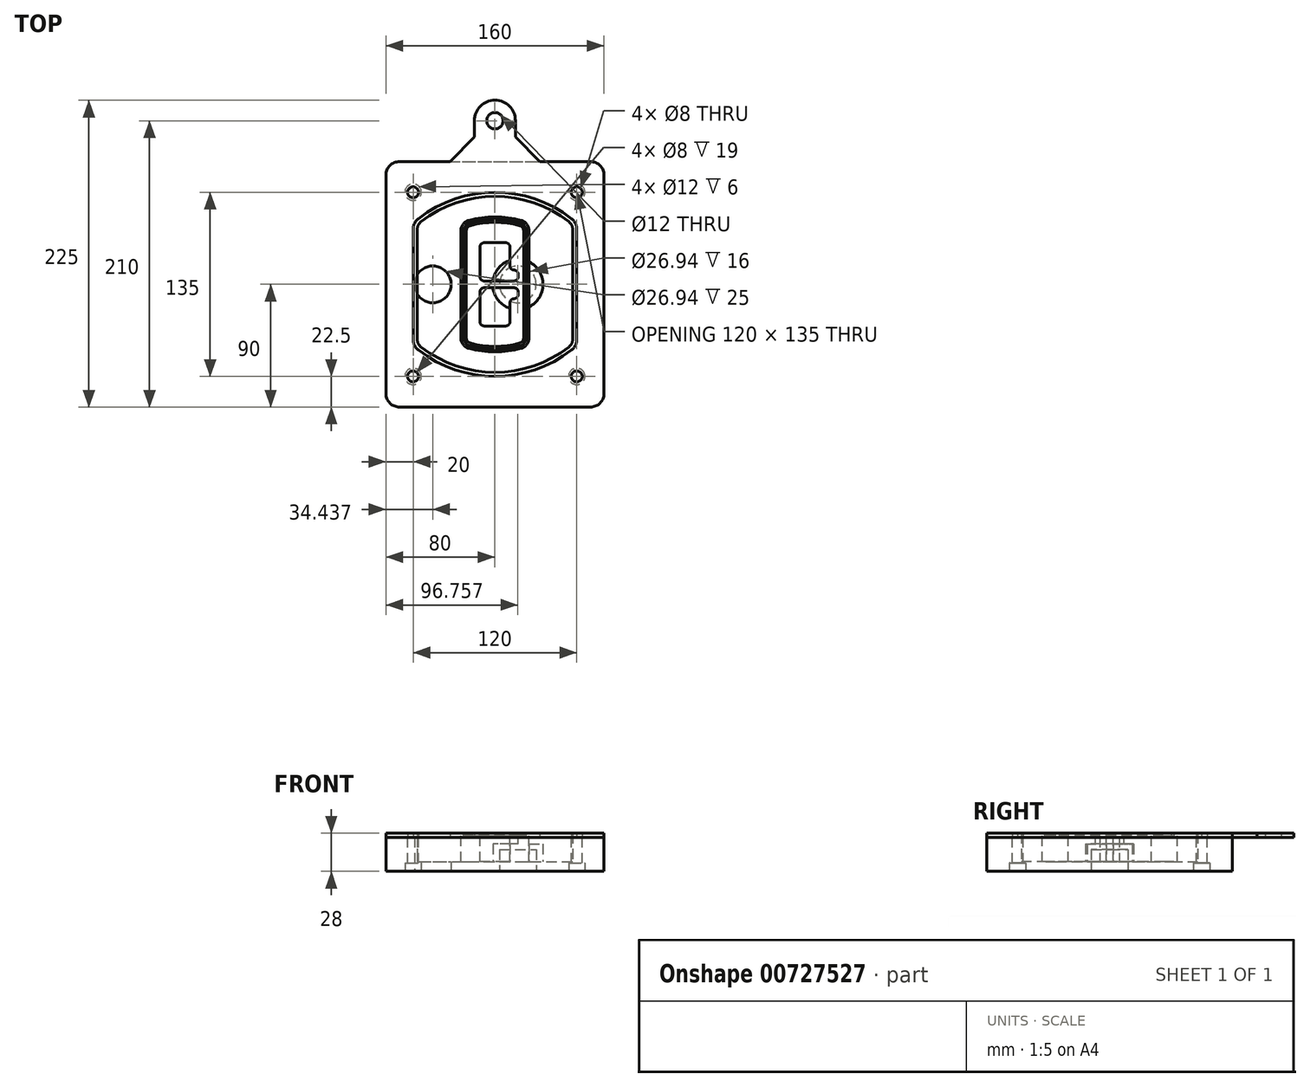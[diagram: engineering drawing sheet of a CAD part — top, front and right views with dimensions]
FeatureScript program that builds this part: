
annotation { "Feature Type Name" : "Feature", "Feature Type Description" : "" }
export const myFeature = defineFeature(function(context is Context, id is Id, definition is map)
    precondition{}
    {
        {
            var Q0;
            Q0=qCreatedBy(makeId("Top.planeOp"),FACE);
            var sketch = newSketch(context, id + "F0", { "sketchPlane" : qUnion([Q0])});
            skPoint(sketch, "E0.rect.middle", {"position": v(0, 0) * mm});
            skLineSegment(sketch, "E1.bottom", {"start": v(-70, -90) * mm, "end": v(70, -90) * mm});
            skLineSegment(sketch, "E1.top", {"start": v(-70, 90) * mm, "end": v(70, 90) * mm});
            skLineSegment(sketch, "E1.left", {"start": v(-80, -80) * mm, "end": v(-80, 80) * mm});
            skLineSegment(sketch, "E1.right", {"start": v(80, -80) * mm, "end": v(80, 80) * mm});
            skLineSegment(sketch, "E2", {"start": v(-80, 90) * mm, "end": v(80, -90) * mm, "construction": true});
            skLineSegment(sketch, "E3", {"start": v(80, 90) * mm, "end": v(-80, -90) * mm, "construction": true});
            skCircle(sketch, "E4", {"center": v(-60, 67.5) * mm, "radius": 4 * mm});
            skCircle(sketch, "E5", {"center": v(60, 67.5) * mm, "radius": 4 * mm});
            skCircle(sketch, "E6", {"center": v(60, -67.5) * mm, "radius": 4 * mm});
            skCircle(sketch, "E7", {"center": v(-60, -67.5) * mm, "radius": 4 * mm});
            skLineSegment(sketch, "E8", {"start": v(-60, 67.5) * mm, "end": v(60, 67.5) * mm, "construction": true});
            skLineSegment(sketch, "E9", {"start": v(60, 67.5) * mm, "end": v(60, -67.5) * mm, "construction": true});
            skLineSegment(sketch, "E10", {"start": v(60, -67.5) * mm, "end": v(-60, -67.5) * mm, "construction": true});
            skLineSegment(sketch, "E11", {"start": v(-60, -67.5) * mm, "end": v(-60, 67.5) * mm, "construction": true});
            skLineSegment(sketch, "E12", {"start": v(-60, 40.3) * mm, "end": v(-60, -40.3) * mm});
            skLineSegment(sketch, "E13", {"start": v(60, 40.3) * mm, "end": v(60, -40.3) * mm});
            skArc(sketch, "E14", {"start": v(56.15, 48.18) * mm, "mid": v(0, 67.5) * mm, "end": v(-56.15, 48.18) * mm});
            skArc(sketch, "E15", {"start": v(-56.15, -48.18) * mm, "mid": v(0, -67.5) * mm, "end": v(56.15, -48.18) * mm});
            skLineSegment(sketch, "E16", {"start": v(-60, 0) * mm, "end": v(60, 0) * mm, "construction": true});
            skPoint(sketch, "E17.visualSharp", {"position": v(-60, -45) * mm});
            skArc(sketch, "E17.filletArc", {"start": v(-60, -40.3) * mm, "mid": v(-58.99, -44.68) * mm, "end": v(-56.15, -48.18) * mm});
            skPoint(sketch, "E18.visualSharp", {"position": v(-60, 45) * mm});
            skArc(sketch, "E18.filletArc", {"start": v(-56.15, 48.18) * mm, "mid": v(-58.99, 44.68) * mm, "end": v(-60, 40.3) * mm});
            skPoint(sketch, "E19.visualSharp", {"position": v(60, 45) * mm});
            skArc(sketch, "E19.filletArc", {"start": v(60, 40.3) * mm, "mid": v(58.99, 44.68) * mm, "end": v(56.15, 48.18) * mm});
            skPoint(sketch, "E20.visualSharp", {"position": v(60, -45) * mm});
            skArc(sketch, "E20.filletArc", {"start": v(56.15, -48.18) * mm, "mid": v(58.99, -44.68) * mm, "end": v(60, -40.3) * mm});
            skPoint(sketch, "E21.visualSharp", {"position": v(-80, 90) * mm});
            skArc(sketch, "E21.filletArc", {"start": v(-70, 90) * mm, "mid": v(-77.07, 87.07) * mm, "end": v(-80, 80) * mm});
            skPoint(sketch, "E22.visualSharp", {"position": v(80, 90) * mm});
            skArc(sketch, "E22.filletArc", {"start": v(80, 80) * mm, "mid": v(77.07, 87.07) * mm, "end": v(70, 90) * mm});
            skPoint(sketch, "E23.visualSharp", {"position": v(80, -90) * mm});
            skArc(sketch, "E23.filletArc", {"start": v(70, -90) * mm, "mid": v(77.07, -87.07) * mm, "end": v(80, -80) * mm});
            skPoint(sketch, "E24.visualSharp", {"position": v(-80, -90) * mm});
            skArc(sketch, "E24.filletArc", {"start": v(-80, -80) * mm, "mid": v(-77.07, -87.07) * mm, "end": v(-70, -90) * mm});
            skArc(sketch, "E25.0", {"start": v(57, 40.3) * mm, "mid": v(56.3, 43.36) * mm, "end": v(54.3, 45.81) * mm});
            skLineSegment(sketch, "E25.1", {"start": v(57, 40.3) * mm, "end": v(57, -40.3) * mm});
            skArc(sketch, "E25.2", {"start": v(54.3, -45.81) * mm, "mid": v(56.3, -43.36) * mm, "end": v(57, -40.3) * mm});
            skArc(sketch, "E25.3", {"start": v(-54.3, -45.81) * mm, "mid": v(0, -64.5) * mm, "end": v(54.3, -45.81) * mm});
            skArc(sketch, "E25.4", {"start": v(-57, -40.3) * mm, "mid": v(-56.3, -43.36) * mm, "end": v(-54.3, -45.81) * mm});
            skArc(sketch, "E25.5", {"start": v(54.3, 45.81) * mm, "mid": v(0, 64.5) * mm, "end": v(-54.3, 45.81) * mm});
            skLineSegment(sketch, "E25.6", {"start": v(-57, 40.3) * mm, "end": v(-57, -40.3) * mm});
            skArc(sketch, "E25.7", {"start": v(-54.3, 45.81) * mm, "mid": v(-56.3, 43.36) * mm, "end": v(-57, 40.3) * mm});
            skArc(sketch, "E26.0", {"start": v(-58.62, 51.33) * mm, "mid": v(-62.58, 46.43) * mm, "end": v(-64, 40.3) * mm});
            skArc(sketch, "E26.1", {"start": v(58.62, 51.33) * mm, "mid": v(0, 71.5) * mm, "end": v(-58.62, 51.33) * mm});
            skArc(sketch, "E26.2", {"start": v(64, 40.3) * mm, "mid": v(62.58, 46.43) * mm, "end": v(58.62, 51.33) * mm});
            skLineSegment(sketch, "E26.3", {"start": v(64, 40.3) * mm, "end": v(64, -40.3) * mm});
            skArc(sketch, "E26.4", {"start": v(58.62, -51.33) * mm, "mid": v(62.58, -46.43) * mm, "end": v(64, -40.3) * mm});
            skLineSegment(sketch, "E26.5", {"start": v(-64, 40.3) * mm, "end": v(-64, -40.3) * mm});
            skArc(sketch, "E26.6", {"start": v(-58.62, -51.33) * mm, "mid": v(0, -71.5) * mm, "end": v(58.62, -51.33) * mm});
            skArc(sketch, "E26.7", {"start": v(-64, -40.3) * mm, "mid": v(-62.58, -46.43) * mm, "end": v(-58.62, -51.33) * mm});
            skSolve(sketch);
        }
        {
            var Q0;
            Q0=makeQuery(id+"F0.imprint","IMPRINT",FACE,{"disambiguationData":[TD([[makeQuery(id+"F0.imprint","IMPRINT",EDGE,{"derivedFrom":sQuery(id+"F0.wireOp",EDGE,"E1.bottom")}),1.0]])]});
            var Q1;
            Q1=makeQuery(id+"F0.imprint","IMPRINT",FACE,{"disambiguationData":[TD([[makeQuery(id+"F0.imprint","IMPRINT",EDGE,{"derivedFrom":sQuery(id+"F0.wireOp",EDGE,"E12")}),1.0]])]});
            var Q2;
            Q2=makeQuery(id+"F0.imprint","IMPRINT",FACE,{"disambiguationData":[TD([[makeQuery(id+"F0.imprint","IMPRINT",EDGE,{"derivedFrom":sQuery(id+"F0.wireOp",EDGE,"E25.0")}),1.0]])]});
            var Q3;
            Q3=makeQuery(id+"F0.imprint","IMPRINT",FACE,{"disambiguationData":[TD([[makeQuery(id+"F0.imprint","IMPRINT",EDGE,{"derivedFrom":sQuery(id+"F0.wireOp",EDGE,"E12")}),-1.0]])]});
            extrude(context, id + "F1", {"entities" : qUnion([Q0, Q1, Q2, Q3]), "oppositeDirection" : true, "depth" : 25 * mm});
        }
        {
            var Q0;
            Q0=makeQuery(id+"F0.imprint","IMPRINT",FACE,{"disambiguationData":[TD([[makeQuery(id+"F0.imprint","IMPRINT",EDGE,{"derivedFrom":sQuery(id+"F0.wireOp",EDGE,"E12")}),1.0]])]});
            extrude(context, id + "F2", {"entities" : qUnion([Q0]), "operationType" : NewBodyOperationType.ADD, "depth" : 3 * mm});
        }
        {
            var Q0;
            Q0=makeQuery(id+"F0.imprint","IMPRINT",FACE,{"disambiguationData":[TD([[makeQuery(id+"F0.imprint","IMPRINT",EDGE,{"derivedFrom":sQuery(id+"F0.wireOp",EDGE,"E25.0")}),1.0]])]});
            extrude(context, id + "F3", {"entities" : qUnion([Q0]), "operationType" : NewBodyOperationType.REMOVE, "oppositeDirection" : true, "depth" : 18 * mm});
        }
        {
            var Q0;
            Q0=makeQuery(id+"F2.opExtrude","CAP_FACE",FACE,{"disambiguationData":[OSD([sQuery(id+"F0.wireOp",EDGE,"E12"),sQuery(id+"F0.wireOp",EDGE,"E13"),sQuery(id+"F0.wireOp",EDGE,"E14"),sQuery(id+"F0.wireOp",EDGE,"E15"),sQuery(id+"F0.wireOp",EDGE,"E17.filletArc"),sQuery(id+"F0.wireOp",EDGE,"E18.filletArc"),sQuery(id+"F0.wireOp",EDGE,"E19.filletArc"),sQuery(id+"F0.wireOp",EDGE,"E20.filletArc"),sQuery(id+"F0.wireOp",EDGE,"E25.0"),sQuery(id+"F0.wireOp",EDGE,"E25.1"),sQuery(id+"F0.wireOp",EDGE,"E25.2"),sQuery(id+"F0.wireOp",EDGE,"E25.3"),sQuery(id+"F0.wireOp",EDGE,"E25.4"),sQuery(id+"F0.wireOp",EDGE,"E25.5"),sQuery(id+"F0.wireOp",EDGE,"E25.6"),sQuery(id+"F0.wireOp",EDGE,"E25.7")])],"isStart":false});
            var sketch = newSketch(context, id + "F4", { "sketchPlane" : qUnion([Q0])});
            skArc(sketch, "E27.0", {"start": v(-19.08, -46.97) * mm, "mid": v(0, -49.5) * mm, "end": v(19.08, -46.97) * mm});
            skArc(sketch, "E28.0", {"start": v(19.08, 46.97) * mm, "mid": v(0, 49.5) * mm, "end": v(-19.08, 46.97) * mm});
            skLineSegment(sketch, "E29", {"start": v(-25, 39.25) * mm, "end": v(-25, -39.25) * mm});
            skLineSegment(sketch, "E30", {"start": v(25, 39.25) * mm, "end": v(25, -39.25) * mm});
            skLineSegment(sketch, "E31", {"start": v(-25, 45.1) * mm, "end": v(25, 45.1) * mm, "construction": true});
            skLineSegment(sketch, "E32", {"start": v(-25, -45.1) * mm, "end": v(25, -45.1) * mm, "construction": true});
            skPoint(sketch, "E33.visualSharp", {"position": v(-25, 45.1) * mm});
            skArc(sketch, "E33.filletArc", {"start": v(-19.08, 46.97) * mm, "mid": v(-23.35, 44.11) * mm, "end": v(-25, 39.25) * mm});
            skPoint(sketch, "E34.visualSharp", {"position": v(25, 45.1) * mm});
            skArc(sketch, "E34.filletArc", {"start": v(25, 39.25) * mm, "mid": v(23.35, 44.11) * mm, "end": v(19.08, 46.97) * mm});
            skPoint(sketch, "E35.visualSharp", {"position": v(25, -45.1) * mm});
            skArc(sketch, "E35.filletArc", {"start": v(19.08, -46.97) * mm, "mid": v(23.35, -44.11) * mm, "end": v(25, -39.25) * mm});
            skPoint(sketch, "E36.visualSharp", {"position": v(-25, -45.1) * mm});
            skArc(sketch, "E36.filletArc", {"start": v(-25, -39.25) * mm, "mid": v(-23.35, -44.11) * mm, "end": v(-19.08, -46.97) * mm});
            skArc(sketch, "E37.0", {"start": v(54.3, 45.81) * mm, "mid": v(0, 64.5) * mm, "end": v(-54.3, 45.81) * mm});
            skArc(sketch, "E37.1", {"start": v(-54.3, 45.81) * mm, "mid": v(-56.3, 43.36) * mm, "end": v(-57, 40.3) * mm});
            skLineSegment(sketch, "E37.2", {"start": v(-57, 40.3) * mm, "end": v(-57, -40.3) * mm});
            skArc(sketch, "E37.3", {"start": v(-57, -40.3) * mm, "mid": v(-56.3, -43.36) * mm, "end": v(-54.3, -45.81) * mm});
            skArc(sketch, "E37.4", {"start": v(-54.3, -45.81) * mm, "mid": v(0, -64.5) * mm, "end": v(54.3, -45.81) * mm});
            skArc(sketch, "E37.5", {"start": v(54.3, -45.81) * mm, "mid": v(56.3, -43.36) * mm, "end": v(57, -40.3) * mm});
            skLineSegment(sketch, "E37.6", {"start": v(57, 40.3) * mm, "end": v(57, -40.3) * mm});
            skArc(sketch, "E37.7", {"start": v(57, 40.3) * mm, "mid": v(56.3, 43.36) * mm, "end": v(54.3, 45.81) * mm});
            skLineSegment(sketch, "E38.0", {"start": v(23, 39.25) * mm, "end": v(23, -39.25) * mm});
            skArc(sketch, "E38.1", {"start": v(18.56, -45.04) * mm, "mid": v(21.76, -42.9) * mm, "end": v(23, -39.25) * mm});
            skArc(sketch, "E38.2", {"start": v(-18.56, -45.04) * mm, "mid": v(0, -47.5) * mm, "end": v(18.56, -45.04) * mm});
            skArc(sketch, "E38.3", {"start": v(-23, -39.25) * mm, "mid": v(-21.76, -42.9) * mm, "end": v(-18.56, -45.04) * mm});
            skLineSegment(sketch, "E38.4", {"start": v(-23, 39.25) * mm, "end": v(-23, -39.25) * mm});
            skArc(sketch, "E38.5", {"start": v(23, 39.25) * mm, "mid": v(21.76, 42.9) * mm, "end": v(18.56, 45.04) * mm});
            skArc(sketch, "E38.6", {"start": v(-18.56, 45.04) * mm, "mid": v(-21.76, 42.9) * mm, "end": v(-23, 39.25) * mm});
            skArc(sketch, "E38.7", {"start": v(18.56, 45.04) * mm, "mid": v(0, 47.5) * mm, "end": v(-18.56, 45.04) * mm});
            skArc(sketch, "E39.0", {"start": v(21, 39.25) * mm, "mid": v(20.18, 41.68) * mm, "end": v(18.04, 43.1) * mm});
            skLineSegment(sketch, "E39.1", {"start": v(21, 39.25) * mm, "end": v(21, -39.25) * mm});
            skArc(sketch, "E39.2", {"start": v(18.04, -43.1) * mm, "mid": v(20.18, -41.68) * mm, "end": v(21, -39.25) * mm});
            skArc(sketch, "E39.3", {"start": v(-18.04, -43.1) * mm, "mid": v(0, -45.5) * mm, "end": v(18.04, -43.1) * mm});
            skArc(sketch, "E39.4", {"start": v(-21, -39.25) * mm, "mid": v(-20.18, -41.68) * mm, "end": v(-18.04, -43.1) * mm});
            skArc(sketch, "E39.5", {"start": v(18.04, 43.1) * mm, "mid": v(0, 45.5) * mm, "end": v(-18.04, 43.1) * mm});
            skLineSegment(sketch, "E39.6", {"start": v(-21, 39.25) * mm, "end": v(-21, -39.25) * mm});
            skArc(sketch, "E39.7", {"start": v(-18.04, 43.1) * mm, "mid": v(-20.18, 41.68) * mm, "end": v(-21, 39.25) * mm});
            skLineSegment(sketch, "E40", {"start": v(-25, 0) * mm, "end": v(25, 0) * mm, "construction": true});
            skLineSegment(sketch, "E41", {"start": v(-11, 5.5) * mm, "end": v(-11, 27.5) * mm});
            skLineSegment(sketch, "E42", {"start": v(-8, 30.5) * mm, "end": v(8, 30.5) * mm});
            skLineSegment(sketch, "E43", {"start": v(11, 27.5) * mm, "end": v(11, 13.5) * mm});
            skLineSegment(sketch, "E44", {"start": v(14, 10.5) * mm, "end": v(14, 10.5) * mm});
            skLineSegment(sketch, "E45", {"start": v(17, 7.5) * mm, "end": v(17, 5.5) * mm});
            skLineSegment(sketch, "E46", {"start": v(14, 2.5) * mm, "end": v(-8, 2.5) * mm});
            skPoint(sketch, "E47.visualSharp", {"position": v(-11, 30.5) * mm});
            skArc(sketch, "E47.filletArc", {"start": v(-8, 30.5) * mm, "mid": v(-10.12, 29.62) * mm, "end": v(-11, 27.5) * mm});
            skPoint(sketch, "E48.visualSharp", {"position": v(11, 30.5) * mm});
            skArc(sketch, "E48.filletArc", {"start": v(11, 27.5) * mm, "mid": v(10.12, 29.62) * mm, "end": v(8, 30.5) * mm});
            skPoint(sketch, "E49.visualSharp", {"position": v(11, 10.5) * mm});
            skArc(sketch, "E49.filletArc", {"start": v(11, 13.5) * mm, "mid": v(11.88, 11.38) * mm, "end": v(14, 10.5) * mm});
            skPoint(sketch, "E50.visualSharp", {"position": v(17, 10.5) * mm});
            skArc(sketch, "E50.filletArc", {"start": v(17, 7.5) * mm, "mid": v(16.12, 9.62) * mm, "end": v(14, 10.5) * mm});
            skPoint(sketch, "E51.visualSharp", {"position": v(17, 2.5) * mm});
            skArc(sketch, "E51.filletArc", {"start": v(14, 2.5) * mm, "mid": v(16.12, 3.38) * mm, "end": v(17, 5.5) * mm});
            skPoint(sketch, "E52.visualSharp", {"position": v(-11, 2.5) * mm});
            skArc(sketch, "E52.filletArc", {"start": v(-11, 5.5) * mm, "mid": v(-10.12, 3.38) * mm, "end": v(-8, 2.5) * mm});
            skLineSegment(sketch, "E53.0.MirrorCS", {"start": v(14, -2.5) * mm, "end": v(-8, -2.5) * mm});
            skArc(sketch, "E54.0.MirrorCS", {"start": v(-11, -5.5) * mm, "mid": v(-10.12, -3.38) * mm, "end": v(-8, -2.5) * mm});
            skLineSegment(sketch, "E55.0.MirrorCS", {"start": v(-11, -5.5) * mm, "end": v(-11, -27.5) * mm});
            skArc(sketch, "E56.0.MirrorCS", {"start": v(-8, -30.5) * mm, "mid": v(-10.12, -29.62) * mm, "end": v(-11, -27.5) * mm});
            skLineSegment(sketch, "E57.0.MirrorCS", {"start": v(-8, -30.5) * mm, "end": v(8, -30.5) * mm});
            skArc(sketch, "E58.0.MirrorCS", {"start": v(11, -27.5) * mm, "mid": v(10.12, -29.62) * mm, "end": v(8, -30.5) * mm});
            skLineSegment(sketch, "E59.0.MirrorCS", {"start": v(11, -27.5) * mm, "end": v(11, -13.5) * mm});
            skArc(sketch, "E60.0.MirrorCS", {"start": v(11, -13.5) * mm, "mid": v(11.88, -11.38) * mm, "end": v(14, -10.5) * mm});
            skArc(sketch, "E61.0.MirrorCS", {"start": v(17, -7.5) * mm, "mid": v(16.12, -9.62) * mm, "end": v(14, -10.5) * mm});
            skLineSegment(sketch, "E62.0.MirrorCS", {"start": v(17, -7.5) * mm, "end": v(17, -5.5) * mm});
            skArc(sketch, "E63.0.MirrorCS", {"start": v(14, -2.5) * mm, "mid": v(16.12, -3.38) * mm, "end": v(17, -5.5) * mm});
            skSolve(sketch);
        }
        {
            var Q0;
            Q0=makeQuery(id+"F4.imprint","IMPRINT",FACE,{"disambiguationData":[TD([[makeQuery(id+"F4.imprint","IMPRINT",EDGE,{"derivedFrom":sQuery(id+"F4.wireOp",EDGE,"E27.0")}),1.0]])]});
            var Q1;
            Q1=makeQuery(id+"F4.imprint","IMPRINT",FACE,{"disambiguationData":[TD([[makeQuery(id+"F4.imprint","IMPRINT",EDGE,{"derivedFrom":sQuery(id+"F4.wireOp",EDGE,"E38.0")}),-1.0]])]});
            var Q2;
            Q2=makeQuery(id+"F4.imprint","IMPRINT",FACE,{"disambiguationData":[TD([[makeQuery(id+"F4.imprint","IMPRINT",EDGE,{"derivedFrom":sQuery(id+"F4.wireOp",EDGE,"E39.0")}),1.0]])]});
            extrude(context, id + "F5", {"entities" : qUnion([Q0, Q1, Q2]), "operationType" : NewBodyOperationType.ADD, "endBound" : BoundingType.UP_TO_NEXT, "oppositeDirection" : true, "depth" : 25 * mm});
        }
        {
            var Q0;
            Q0=makeQuery(id+"F4.imprint","IMPRINT",FACE,{"disambiguationData":[TD([[makeQuery(id+"F4.imprint","IMPRINT",EDGE,{"derivedFrom":sQuery(id+"F4.wireOp",EDGE,"E38.0")}),-1.0]])]});
            extrude(context, id + "F6", {"entities" : qUnion([Q0]), "operationType" : NewBodyOperationType.REMOVE, "oppositeDirection" : true, "depth" : 2 * mm});
        }
        {
            var Q0;
            Q0=makeQuery(id+"F1.opExtrude","CAP_FACE",FACE,{"disambiguationData":[OSD([sQuery(id+"F0.wireOp",EDGE,"E1.bottom"),sQuery(id+"F0.wireOp",EDGE,"E1.top"),sQuery(id+"F0.wireOp",EDGE,"E1.left"),sQuery(id+"F0.wireOp",EDGE,"E1.right"),sQuery(id+"F0.wireOp",EDGE,"E4"),sQuery(id+"F0.wireOp",EDGE,"E5"),sQuery(id+"F0.wireOp",EDGE,"E6"),sQuery(id+"F0.wireOp",EDGE,"E7"),sQuery(id+"F0.wireOp",EDGE,"E21.filletArc"),sQuery(id+"F0.wireOp",EDGE,"E22.filletArc"),sQuery(id+"F0.wireOp",EDGE,"E23.filletArc"),sQuery(id+"F0.wireOp",EDGE,"E24.filletArc")])],"isStart":false});
            var sketch = newSketch(context, id + "F7", { "sketchPlane" : qUnion([Q0])});
            skCircle(sketch, "E64", {"center": v(16.76, 0) * mm, "radius": 13.47 * mm});
            skCircle(sketch, "E65", {"center": v(-45.56, 0) * mm, "radius": 13.47 * mm});
            skLineSegment(sketch, "E66", {"start": v(80, 0) * mm, "end": v(-80, 0) * mm});
            skCircle(sketch, "E67", {"center": v(16.76, 0) * mm, "radius": 18.47 * mm});
            skCircle(sketch, "E68", {"center": v(60, -67.5) * mm, "radius": 6 * mm});
            skCircle(sketch, "E69", {"center": v(-60, -67.5) * mm, "radius": 6 * mm});
            skCircle(sketch, "E70", {"center": v(-60, 67.5) * mm, "radius": 6 * mm});
            skCircle(sketch, "E71", {"center": v(60, 67.5) * mm, "radius": 6 * mm});
            skSolve(sketch);
        }
        {
            var Q0;
            {var subQ1=sQuery(id+"F7.wireOp",EDGE,"E66");var subQ4=sQuery(id+"F7.wireOp",EDGE,"E64");var subQ6=makeQuery(id+"F7.imprint","INTERSECT",VERTEX,{"disambiguationData":[OD(0.0)],"derivedFrom":[subQ4,subQ1]});Q0=makeQuery(id+"F7.imprint","IMPRINT",FACE,{"disambiguationData":[TD([[makeQuery(id+"F7.imprint","IMPRINT",EDGE,{"disambiguationData":[TD([[subQ6,-1.0]])],"derivedFrom":subQ4}),-1.0]])]});}
            var Q1;
            {var subQ0=sQuery(id+"F7.wireOp",EDGE,"E66");var subQ1=sQuery(id+"F7.wireOp",EDGE,"E64");var subQ3=makeQuery(id+"F7.imprint","INTERSECT",VERTEX,{"disambiguationData":[OD(0.0)],"derivedFrom":[subQ1,subQ0]});Q1=makeQuery(id+"F7.imprint","IMPRINT",FACE,{"disambiguationData":[TD([[makeQuery(id+"F7.imprint","IMPRINT",EDGE,{"disambiguationData":[TD([[subQ3,-1.0]])],"derivedFrom":subQ1}),1.0]])]});}
            var Q2;
            {var subQ0=sQuery(id+"F7.wireOp",EDGE,"E66");var subQ1=sQuery(id+"F7.wireOp",EDGE,"E64");var subQ3=makeQuery(id+"F7.imprint","INTERSECT",VERTEX,{"disambiguationData":[OD(0.0)],"derivedFrom":[subQ1,subQ0]});Q2=makeQuery(id+"F7.imprint","IMPRINT",FACE,{"disambiguationData":[TD([[makeQuery(id+"F7.imprint","IMPRINT",EDGE,{"disambiguationData":[TD([[subQ3,1.0]])],"derivedFrom":subQ1}),1.0]])]});}
            var Q3;
            {var subQ1=sQuery(id+"F7.wireOp",EDGE,"E66");var subQ4=sQuery(id+"F7.wireOp",EDGE,"E64");var subQ6=makeQuery(id+"F7.imprint","INTERSECT",VERTEX,{"disambiguationData":[OD(0.0)],"derivedFrom":[subQ4,subQ1]});Q3=makeQuery(id+"F7.imprint","IMPRINT",FACE,{"disambiguationData":[TD([[makeQuery(id+"F7.imprint","IMPRINT",EDGE,{"disambiguationData":[TD([[subQ6,1.0]])],"derivedFrom":subQ4}),-1.0]])]});}
            extrude(context, id + "F8", {"entities" : qUnion([Q0, Q1, Q2, Q3]), "operationType" : NewBodyOperationType.ADD, "oppositeDirection" : true, "depth" : 20 * mm});
        }
        {
            var Q0;
            {var subQ0=sQuery(id+"F7.wireOp",EDGE,"E66");var subQ1=sQuery(id+"F7.wireOp",EDGE,"E64");var subQ3=makeQuery(id+"F7.imprint","INTERSECT",VERTEX,{"disambiguationData":[OD(0.0)],"derivedFrom":[subQ1,subQ0]});Q0=makeQuery(id+"F7.imprint","IMPRINT",FACE,{"disambiguationData":[TD([[makeQuery(id+"F7.imprint","IMPRINT",EDGE,{"disambiguationData":[TD([[subQ3,-1.0]])],"derivedFrom":subQ1}),1.0]])]});}
            var Q1;
            {var subQ0=sQuery(id+"F7.wireOp",EDGE,"E66");var subQ1=sQuery(id+"F7.wireOp",EDGE,"E64");var subQ3=makeQuery(id+"F7.imprint","INTERSECT",VERTEX,{"disambiguationData":[OD(0.0)],"derivedFrom":[subQ1,subQ0]});Q1=makeQuery(id+"F7.imprint","IMPRINT",FACE,{"disambiguationData":[TD([[makeQuery(id+"F7.imprint","IMPRINT",EDGE,{"disambiguationData":[TD([[subQ3,1.0]])],"derivedFrom":subQ1}),1.0]])]});}
            extrude(context, id + "F9", {"entities" : qUnion([Q0, Q1]), "operationType" : NewBodyOperationType.REMOVE, "oppositeDirection" : true, "depth" : 16 * mm});
        }
        {
            var Q0;
            {var subQ0=sQuery(id+"F7.wireOp",EDGE,"E66");var subQ1=sQuery(id+"F7.wireOp",EDGE,"E65");var subQ3=makeQuery(id+"F7.imprint","INTERSECT",VERTEX,{"disambiguationData":[OD(0.0)],"derivedFrom":[subQ1,subQ0]});Q0=makeQuery(id+"F7.imprint","IMPRINT",FACE,{"disambiguationData":[TD([[makeQuery(id+"F7.imprint","IMPRINT",EDGE,{"disambiguationData":[TD([[subQ3,-1.0]])],"derivedFrom":subQ1}),1.0]])]});}
            var Q1;
            {var subQ0=sQuery(id+"F7.wireOp",EDGE,"E66");var subQ1=sQuery(id+"F7.wireOp",EDGE,"E65");var subQ3=makeQuery(id+"F7.imprint","INTERSECT",VERTEX,{"disambiguationData":[OD(0.0)],"derivedFrom":[subQ1,subQ0]});Q1=makeQuery(id+"F7.imprint","IMPRINT",FACE,{"disambiguationData":[TD([[makeQuery(id+"F7.imprint","IMPRINT",EDGE,{"disambiguationData":[TD([[subQ3,1.0]])],"derivedFrom":subQ1}),1.0]])]});}
            extrude(context, id + "F10", {"entities" : qUnion([Q0, Q1]), "operationType" : NewBodyOperationType.REMOVE, "oppositeDirection" : true, "depth" : 25 * mm});
        }
        {
            var Q0;
            Q0=makeQuery(id+"F7.imprint","IMPRINT",FACE,{"disambiguationData":[TD([[makeQuery(id+"F7.imprint","IMPRINT",EDGE,{"derivedFrom":sQuery(id+"F7.wireOp",EDGE,"E68")}),1.0]])]});
            var Q1;
            Q1=makeQuery(id+"F7.imprint","IMPRINT",FACE,{"disambiguationData":[TD([[makeQuery(id+"F7.imprint","IMPRINT",EDGE,{"derivedFrom":makeQuery(id+"F1.opExtrude","CAP_EDGE",EDGE,{"disambiguationData":[OSD([sQuery(id+"F0.wireOp",EDGE,"E5")])],"isStart":false})}),-1.0]])]});
            var Q2;
            Q2=makeQuery(id+"F7.imprint","IMPRINT",FACE,{"disambiguationData":[TD([[makeQuery(id+"F7.imprint","IMPRINT",EDGE,{"derivedFrom":sQuery(id+"F7.wireOp",EDGE,"E69")}),1.0]])]});
            var Q3;
            Q3=makeQuery(id+"F7.imprint","IMPRINT",FACE,{"disambiguationData":[TD([[makeQuery(id+"F7.imprint","IMPRINT",EDGE,{"derivedFrom":makeQuery(id+"F1.opExtrude","CAP_EDGE",EDGE,{"disambiguationData":[OSD([sQuery(id+"F0.wireOp",EDGE,"E4")])],"isStart":false})}),-1.0]])]});
            var Q4;
            Q4=makeQuery(id+"F7.imprint","IMPRINT",FACE,{"disambiguationData":[TD([[makeQuery(id+"F7.imprint","IMPRINT",EDGE,{"derivedFrom":sQuery(id+"F7.wireOp",EDGE,"E70")}),1.0]])]});
            var Q5;
            Q5=makeQuery(id+"F7.imprint","IMPRINT",FACE,{"disambiguationData":[TD([[makeQuery(id+"F7.imprint","IMPRINT",EDGE,{"derivedFrom":makeQuery(id+"F1.opExtrude","CAP_EDGE",EDGE,{"disambiguationData":[OSD([sQuery(id+"F0.wireOp",EDGE,"E7")])],"isStart":false})}),-1.0]])]});
            var Q6;
            Q6=makeQuery(id+"F7.imprint","IMPRINT",FACE,{"disambiguationData":[TD([[makeQuery(id+"F7.imprint","IMPRINT",EDGE,{"derivedFrom":sQuery(id+"F7.wireOp",EDGE,"E71")}),1.0]])]});
            var Q7;
            Q7=makeQuery(id+"F7.imprint","IMPRINT",FACE,{"disambiguationData":[TD([[makeQuery(id+"F7.imprint","IMPRINT",EDGE,{"derivedFrom":makeQuery(id+"F1.opExtrude","CAP_EDGE",EDGE,{"disambiguationData":[OSD([sQuery(id+"F0.wireOp",EDGE,"E6")])],"isStart":false})}),-1.0]])]});
            extrude(context, id + "F11", {"entities" : qUnion([Q0, Q1, Q2, Q3, Q4, Q5, Q6, Q7]), "operationType" : NewBodyOperationType.REMOVE, "oppositeDirection" : true, "depth" : 6 * mm});
        }
        {
            var Q0;
            {var subQ0=sQuery(id+"F0.wireOp",EDGE,"E21.filletArc");var subQ1=sQuery(id+"F0.wireOp",EDGE,"E7");var subQ2=sQuery(id+"F0.wireOp",EDGE,"E6");var subQ3=sQuery(id+"F0.wireOp",EDGE,"E5");var subQ4=sQuery(id+"F0.wireOp",EDGE,"E4");var subQ5=sQuery(id+"F0.wireOp",EDGE,"E22.filletArc");var subQ6=sQuery(id+"F0.wireOp",EDGE,"E1.bottom");var subQ7=sQuery(id+"F0.wireOp",EDGE,"E1.right");var subQ8=sQuery(id+"F0.wireOp",EDGE,"E1.top");var subQ9=sQuery(id+"F0.wireOp",EDGE,"E1.left");var subQ10=sQuery(id+"F0.wireOp",EDGE,"E23.filletArc");var subQ11=sQuery(id+"F0.wireOp",EDGE,"E24.filletArc");Q0=makeQuery(id+"F2.boolean.opBoolean","SPLIT",FACE,{"disambiguationData":[TD([makeQuery(id+"F1.opExtrude","SWEPT_FACE",FACE,{"disambiguationData":[OSD([subQ6])]})])],"derivedFrom":makeQuery(id+"F1.opExtrude","CAP_FACE",FACE,{"disambiguationData":[OSD([subQ6,subQ8,subQ9,subQ7,subQ4,subQ3,subQ2,subQ1,subQ0,subQ5,subQ10,subQ11])],"isStart":true})});}
            var sketch = newSketch(context, id + "F12", { "sketchPlane" : qUnion([Q0])});
            skLineSegment(sketch, "E72", {"start": v(0, 90) * mm, "end": v(0, 120) * mm, "construction": true});
            skCircle(sketch, "E73", {"center": v(0, 120) * mm, "radius": 6 * mm});
            skLineSegment(sketch, "E74", {"start": v(-33, 90) * mm, "end": v(-15, 108) * mm});
            skLineSegment(sketch, "E75", {"start": v(-15, 108) * mm, "end": v(-15, 120) * mm});
            skLineSegment(sketch, "E76", {"start": v(33, 90) * mm, "end": v(15, 108) * mm});
            skLineSegment(sketch, "E77", {"start": v(15, 108) * mm, "end": v(15, 120) * mm});
            skArc(sketch, "E78", {"start": v(15, 120) * mm, "mid": v(0, 135) * mm, "end": v(-15, 120) * mm});
            skLineSegment(sketch, "E79", {"start": v(-80, 0) * mm, "end": v(80, 0) * mm, "construction": true});
            skArc(sketch, "E80.MirrorCS", {"start": v(15, -120) * mm, "mid": v(0, -135) * mm, "end": v(-15, -120) * mm});
            skLineSegment(sketch, "E81.MirrorCS", {"start": v(-15, -108) * mm, "end": v(-15, -120) * mm});
            skLineSegment(sketch, "E82.MirrorCS", {"start": v(15, -108) * mm, "end": v(15, -120) * mm});
            skCircle(sketch, "E83.MirrorC", {"center": v(0, -120) * mm, "radius": 6 * mm});
            skLineSegment(sketch, "E84.MirrorCS", {"start": v(0, -90) * mm, "end": v(0, -120) * mm, "construction": true});
            skLineSegment(sketch, "E85.MirrorCS", {"start": v(-33, -90) * mm, "end": v(-15, -108) * mm});
            skLineSegment(sketch, "E86.MirrorCS", {"start": v(33, -90) * mm, "end": v(15, -108) * mm});
            skSolve(sketch);
        }
        {
            var Q0;
            Q0=makeQuery(id+"F12.imprint","IMPRINT",FACE,{"disambiguationData":[TD([[makeQuery(id+"F12.imprint","IMPRINT",EDGE,{"derivedFrom":sQuery(id+"F12.wireOp",EDGE,"E73")}),-1.0]])]});
            var Q1;
            Q1=makeQuery(id+"F12.imprint","IMPRINT",FACE,{"disambiguationData":[TD([[makeQuery(id+"F12.imprint","IMPRINT",EDGE,{"derivedFrom":sQuery(id+"F12.wireOp",EDGE,"E80.MirrorCS")}),-1.0]])]});
            var Q2;
            Q2=makeQuery(id+"F12.imprint","IMPRINT",FACE,{"disambiguationData":[TD([[makeQuery(id+"F12.imprint","IMPRINT",EDGE,{"derivedFrom":makeQuery(id+"F1.opExtrude","CAP_EDGE",EDGE,{"disambiguationData":[OSD([sQuery(id+"F0.wireOp",EDGE,"E1.left")])],"isStart":true})}),-1.0]])]});
            var Q3;
            Q3=makeQuery(id+"F2.opExtrude","CAP_FACE",FACE,{"disambiguationData":[OSD([sQuery(id+"F0.wireOp",EDGE,"E12"),sQuery(id+"F0.wireOp",EDGE,"E13"),sQuery(id+"F0.wireOp",EDGE,"E14"),sQuery(id+"F0.wireOp",EDGE,"E15"),sQuery(id+"F0.wireOp",EDGE,"E17.filletArc"),sQuery(id+"F0.wireOp",EDGE,"E18.filletArc"),sQuery(id+"F0.wireOp",EDGE,"E19.filletArc"),sQuery(id+"F0.wireOp",EDGE,"E20.filletArc"),sQuery(id+"F0.wireOp",EDGE,"E25.0"),sQuery(id+"F0.wireOp",EDGE,"E25.1"),sQuery(id+"F0.wireOp",EDGE,"E25.2"),sQuery(id+"F0.wireOp",EDGE,"E25.3"),sQuery(id+"F0.wireOp",EDGE,"E25.4"),sQuery(id+"F0.wireOp",EDGE,"E25.5"),sQuery(id+"F0.wireOp",EDGE,"E25.6"),sQuery(id+"F0.wireOp",EDGE,"E25.7")])],"isStart":false});
            extrude(context, id + "F13", {"entities" : qUnion([Q0, Q1, Q2]), "endBound" : BoundingType.UP_TO_SURFACE, "depth" : 25 * mm, "endBoundEntityFace" : qUnion([Q3]), "offsetDistance" : 25 * mm});
        }
    });
